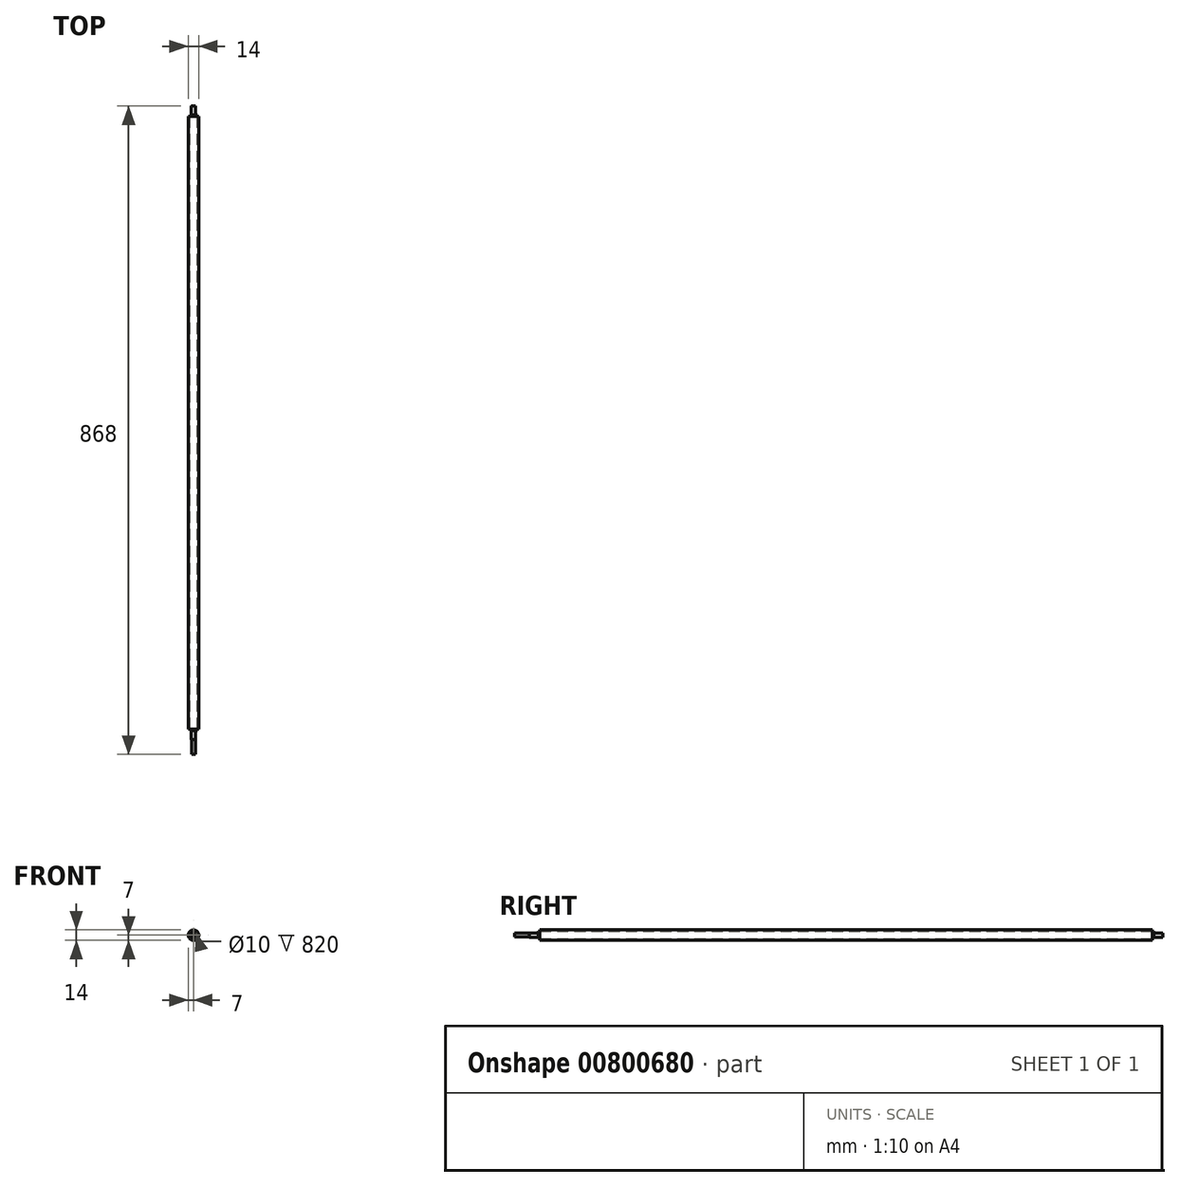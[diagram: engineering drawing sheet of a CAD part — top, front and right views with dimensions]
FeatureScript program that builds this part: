
annotation { "Feature Type Name" : "Feature", "Feature Type Description" : "" }
export const myFeature = defineFeature(function(context is Context, id is Id, definition is map)
    precondition{}
    {
        {
            var Q0;
            Q0=qCreatedBy(makeId("Front.planeOp"),FACE);
            var sketch = newSketch(context, id + "F0", { "sketchPlane" : qUnion([Q0])});
            skCircle(sketch, "E0", {"center": v(0, 0) * mm, "radius": 5 * mm});
            skSolve(sketch);
        }
        {
            var Q0;
            Q0 = qSketchRegion(id + "F0", true);
            extrude(context, id + "F1", {"entities" : qUnion([Q0]), "endBound" : BoundingType.SYMMETRIC, "depth" : 824 * mm, "offsetDistance" : 25 * mm});
        }
        {
            var Q0;
            Q0=makeQuery(id+"F1.opExtrude","CAP_FACE",FACE,{"disambiguationData":[OSD([sQuery(id+"F0.wireOp",EDGE,"E0")])],"isStart":false});
            var sketch = newSketch(context, id + "F2", { "sketchPlane" : qUnion([Q0])});
            skCircle(sketch, "E1", {"center": v(0, 0) * mm, "radius": 3 * mm});
            skSolve(sketch);
        }
        {
            var Q0;
            Q0 = qSketchRegion(id + "F2", true);
            extrude(context, id + "F3", {"entities" : qUnion([Q0]), "operationType" : NewBodyOperationType.ADD, "depth" : 12 * mm, "offsetDistance" : 25 * mm});
        }
        {
            var Q0;
            Q0=makeQuery(id+"F1.opExtrude","CAP_FACE",FACE,{"disambiguationData":[OSD([sQuery(id+"F0.wireOp",EDGE,"E0")])],"isStart":true});
            var sketch = newSketch(context, id + "F4", { "sketchPlane" : qUnion([Q0])});
            skCircle(sketch, "E2", {"center": v(0, 0) * mm, "radius": 3 * mm});
            skSolve(sketch);
        }
        {
            var Q0;
            Q0 = qSketchRegion(id + "F4", true);
            extrude(context, id + "F5", {"entities" : qUnion([Q0]), "operationType" : NewBodyOperationType.ADD, "depth" : 12 * mm, "offsetDistance" : 25 * mm});
        }
        {
            var Q0;
            Q0=makeQuery(id+"F1.opExtrude","CAP_FACE",FACE,{"disambiguationData":[OSD([sQuery(id+"F0.wireOp",EDGE,"E0")])],"isStart":true});
            var sketch = newSketch(context, id + "F6", { "sketchPlane" : qUnion([Q0])});
            skCircle(sketch, "E3.0", {"center": v(0, 0) * mm, "radius": 5 * mm});
            skCircle(sketch, "E4", {"center": v(0, 0) * mm, "radius": 7 * mm});
            skSolve(sketch);
        }
        {
            var Q0;
            Q0 = qSketchRegion(id + "F6", true);
            var Q1;
            Q1=makeQuery(id+"F1.opExtrude","CAP_FACE",FACE,{"disambiguationData":[OSD([sQuery(id+"F0.wireOp",EDGE,"E0")])],"isStart":false});
            extrude(context, id + "F7", {"entities" : qUnion([Q0]), "endBound" : BoundingType.UP_TO_SURFACE, "oppositeDirection" : true, "depth" : 25 * mm, "endBoundEntityFace" : qUnion([Q1]), "offsetDistance" : 25 * mm});
        }
        {
            var Q0;
            Q0=makeQuery(id+"F3.opExtrude","CAP_FACE",FACE,{"disambiguationData":[OSD([sQuery(id+"F2.wireOp",EDGE,"E1")])],"isStart":false});
            var sketch = newSketch(context, id + "F8", { "sketchPlane" : qUnion([Q0])});
            skCircle(sketch, "E5", {"center": v(0, 0) * mm, "radius": 2.5 * mm});
            skSolve(sketch);
        }
        {
            var Q0;
            Q0 = qSketchRegion(id + "F8", true);
            extrude(context, id + "F9", {"entities" : qUnion([Q0]), "operationType" : NewBodyOperationType.ADD, "depth" : 20 * mm, "offsetDistance" : 25 * mm});
        }
        {
            var Q0;
            Q0=makeQuery(id+"F7.opExtrude","CAP_FACE",FACE,{"disambiguationData":[OSD([sQuery(id+"F6.wireOp",EDGE,"E3.0"),sQuery(id+"F6.wireOp",EDGE,"E4")])],"isStart":true});
            extrude(context, id + "F10", {"entities" : qUnion([Q0]), "operationType" : NewBodyOperationType.REMOVE, "oppositeDirection" : true, "depth" : 2 * mm, "offsetDistance" : 25 * mm});
        }
        {
            var Q0;
            Q0=makeQuery(id+"F7.opExtrude","CAP_FACE",FACE,{"disambiguationData":[OSD([sQuery(id+"F6.wireOp",EDGE,"E3.0"),sQuery(id+"F6.wireOp",EDGE,"E4")])],"isStart":false});
            extrude(context, id + "F11", {"entities" : qUnion([Q0]), "operationType" : NewBodyOperationType.REMOVE, "oppositeDirection" : true, "depth" : 2 * mm, "offsetDistance" : 25 * mm});
        }
    });
